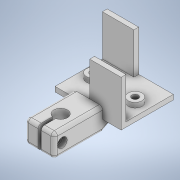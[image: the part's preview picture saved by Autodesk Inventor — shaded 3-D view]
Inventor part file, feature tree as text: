
AUTODESK INVENTOR PART (.ipt)
format: ipt  version: 2020 (Build 240168000, 168)  size: 277,504 bytes
history: native  units: in
note: dims shown in document units (in); Inventor stores cm internally (conversion verified against a paired STEP export)
features: extrude x13, sketch x13, fillet x2, mirror x1
ambient origin geometry x8: Origin, YZ Plane, XZ Plane, XY Plane, X Axis, Y Axis, Z Axis, Center Point
bodies: Solid1 (feature_tree)
feature tree (29):
  extrude  "Extrusion1"  Depth=1.2756in
  extrude  "Extrusion3"  Depth=0.1181in
  extrude  "Extrusion4"  Depth=1.0in TaperAngle=0.0deg
  extrude  "Extrusion5"  Depth=0.1181in TaperAngle=0.0deg
  extrude  "Extrusion6"  Depth=0.1181in TaperAngle=0.0deg
  extrude  "Extrusion7"  Depth=0.3346in
  extrude  "Extrusion8"  Depth=0.1575in
  extrude  "Extrusion9"  Depth=0.2362in TaperAngle=0.0deg
  extrude  "Extrusion10"  Depth=0.2362in
  extrude  "Extrusion11"  Depth=0.7087in
  extrude  "Extrusion12"  Depth=1.1811in TaperAngle=0.0deg
  extrude  "Extrusion13"  Depth=0.1181in
  mirror  "Mirror1"
  extrude  "Extrusion14"  Depth=0.0787in TaperAngle=0.0deg
  fillet  "Fillet1"  Radius=0.3346in
  fillet  "Fillet2"  Radius=0.0787in
  sketch  "Sketch1"  dims[d0=1.6142in d1=1.2756in]
  sketch  "Sketch3"  dims[d2=0.1181in d3=0.0in d8=0.1181in]
  sketch  "Sketch4"  dims[d9=0.1181in d10=1.0in d11=0.0in]
  sketch  "Sketch5"  dims[d12=0.8465in d13=0.1181in d14=0.0in]
  sketch  "Sketch6"  dims[d15=0.8465in d16=0.1181in d17=0.0in]
  sketch  "Sketch7"  dims[d20=0.3346in d21=0.3346in]
  sketch  "Sketch8"  dims[d22=0.1181in d23=0.0in d24=0.1575in]
  sketch  "Sketch9"  dims[d25=0.1575in d26=0.2362in d27=0.0in]
  sketch  "Sketch10"  dims[d28=0.2362in d29=0.2362in]
  sketch  "Sketch11"  dims[d30=0.1181in d31=0.0in d32=0.7087in]
  sketch  "Sketch12"  dims[d33=0.5512in d34=1.1811in d35=0.0in]
  sketch  "Sketch13"  dims[d36=0.1181in d37=0.1181in]
  sketch  "Sketch14"  dims[d38=0.2756in d39=0.0in d40=0.7087in d41=0.0in d42=0.3346in d43=0.0787in d44=1.1811in d45=0.0in d46=0.2362in d47=0.1181in d48=0.0in d49=0.1575in d50=0.7874in d51=0.0in d52=0.0787in d53=0.0787in]
